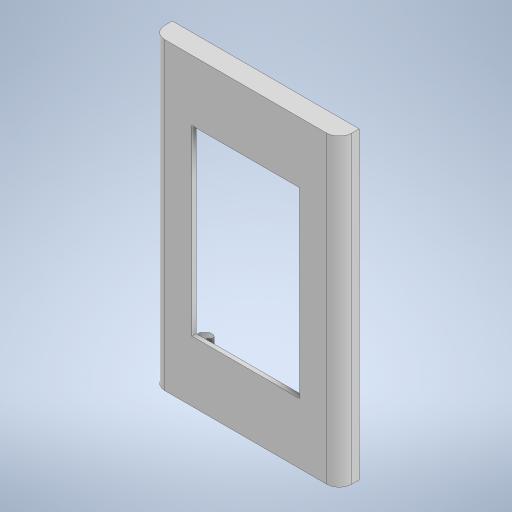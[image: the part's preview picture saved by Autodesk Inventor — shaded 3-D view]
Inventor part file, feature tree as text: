
AUTODESK INVENTOR PART (.ipt)
format: ipt  version: 2023 (Build 270158000, 158)  size: 295,424 bytes
history: native  units: mm
features: extrude x4, sketch x4, mirror x2, other x1, fillet x1, shell x1, chamfer x1
ambient origin geometry x8: Origin, YZ Plane, XZ Plane, XY Plane, X Axis, Y Axis, Z Axis, Center Point
bodies: Body1 (feature_tree)
feature tree (14):
  other  "솔리드1"
  extrude  "돌출1"  Depth=75.0mm
  fillet  "모깎기1"  Radius=122.0mm
  shell  "쉘1"  Thickness=43.2mm
  extrude  "돌출2"  Depth=73.2mm
  extrude  "돌출3"  Depth=8.0mm TaperAngle=0.0deg
  chamfer  "모따기1"  Distance=5.0mm
  extrude  "돌출4"  Depth=1.7mm
  mirror  "미러1"
  mirror  "미러2"
  sketch  "스케치1"
  sketch  "스케치2"
  sketch  "스케치3"
  sketch  "스케치4"
